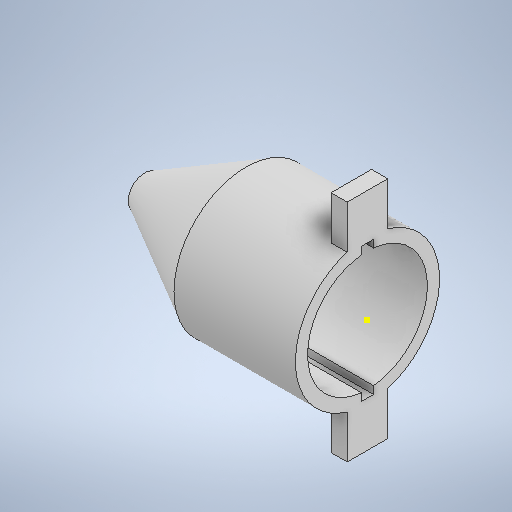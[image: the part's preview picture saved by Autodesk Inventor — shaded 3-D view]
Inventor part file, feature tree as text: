
AUTODESK INVENTOR PART (.ipt)
format: ipt  version: 2025.2 (Build 292293000, 293)  size: 333,312 bytes
history: native  units: in
note: dims shown in document units (in); Inventor stores cm internally (conversion verified against a paired STEP export)
features: sketch x19, extrude x10, revolve x1, thread x1
ambient origin geometry x8: Origin, YZ Plane, XZ Plane, XY Plane, X Axis, Y Axis, Z Axis, Center Point
bodies: Solid1 (feature_tree)
feature tree (31):
  revolve  "Revolution1"  Angle=90.0deg
  sketch  "Sketch2"  dims[d2=0.3937in d3=0.0in d6=0.5906in d7=0.0in]
  sketch  "Sketch3"  dims[d8=0.1772in d9=0.0787in]
  sketch  "Sketch4"  dims[d10=0.1181in d11=0.0in d12=0.5906in]
  sketch  "Sketch5"  dims[d13=0.0787in d14=0.0591in]
  extrude  "Extrusion1"  Depth=0.5906in TaperAngle=0.0deg
  sketch  "Sketch6"  dims[d15=0.3937in d16=0.0in d17=0.3937in d18=0.0in]
  extrude  "Extrusion2"  Depth=0.0787in
  extrude  "Extrusion3"  Depth=0.5906in
  sketch  "Sketch9"  dims[d25=0.5906in d26=0.0in d29=0.1969in]
  sketch  "Sketch10"  dims[d30=0.0984in d31=0.0787in d32=0.0in]
  sketch  "Sketch11"  dims[d33=0.0354in d34=0.0295in d35=0.3937in d36=0.0in]
  sketch  "Sketch12"  dims[d37=0.1181in]
  sketch  "Sketch13"  dims[d38=0.3937in d39=0.0in]
  extrude  "Extrusion4"  Depth=0.0591in
  extrude  "Extrusion5"  Depth=0.3937in TaperAngle=0.0deg
  extrude  "Extrusion6"  Depth=0.3937in TaperAngle=0.0deg
  extrude  "Extrusion7"  Depth=0.0591in
  extrude  "Extrusion8"  Depth=0.1969in
  sketch  "Sketch16"
  extrude  "Extrusion9"  Depth=0.0787in TaperAngle=0.0deg
  extrude  "Extrusion10"  Depth=0.3937in
  sketch  "Sketch19"
  thread  "Thread3"  [1 undecoded]
  sketch  "Sketch1"  dims[d0=0.0787in d1=90.0deg]
  sketch  "Sketch7"  dims[d19=0.3937in d20=0.0in d21=0.3937in d22=0.0in]
  sketch  "Sketch8"  dims[d23=0.0591in d24=0.0591in]
  sketch  "Sketch14"
  sketch  "Sketch15"
  sketch  "Sketch17"
  sketch  "Sketch18"
note: 1 required parameter value undecoded (feature->parameter linkage not recoverable at this tier; creation-order binding heuristic only, values carry confidence <= 0.55)
